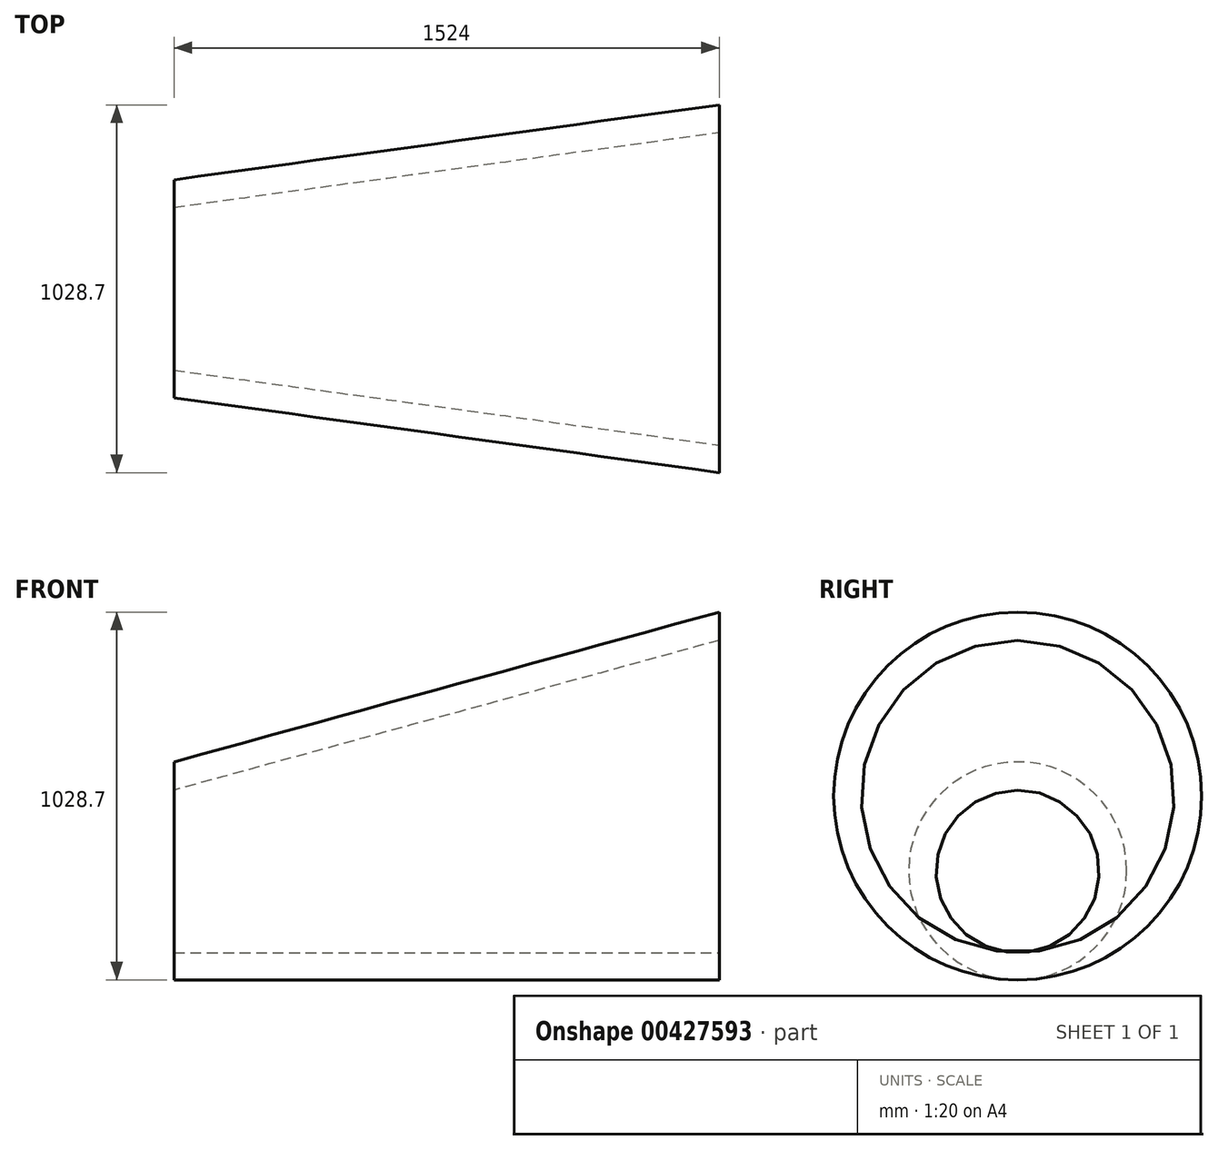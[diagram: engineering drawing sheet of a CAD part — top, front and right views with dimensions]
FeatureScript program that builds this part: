
annotation { "Feature Type Name" : "Feature", "Feature Type Description" : "" }
export const myFeature = defineFeature(function(context is Context, id is Id, definition is map)
    precondition{}
    {
        {
            var Q0;
            Q0=qCreatedBy(makeId("Right.planeOp"),FACE);
            var sketch = newSketch(context, id + "F0", { "sketchPlane" : qUnion([Q0])});
            skCircle(sketch, "E0", {"center": v(0, 0) * mm, "radius": 304.8 * mm});
            skPoint(sketch, "E1", {"position": v(0, -304.8) * mm});
            skLineSegment(sketch, "E2", {"start": v(0, 0) * mm, "end": v(0, -304.8) * mm, "construction": true});
            skSolve(sketch);
        }
        {
            var Q0;
            Q0=makeQuery(id+"F0.imprint","IMPRINT",FACE,{"disambiguationData":[TD([[makeQuery(id+"F0.imprint","IMPRINT",EDGE,{"derivedFrom":sQuery(id+"F0.wireOp",EDGE,"E0")}),1.0]])]});
            cPlane(context, id + "F1", {"entities" : qUnion([Q0]), "cplaneType" : CPlaneType.OFFSET, "offset" : 1524 * mm, "width" : 152.4 * mm, "height" : 152.4 * mm});
        }
        {
            var Q0;
            Q0=qCreatedBy(id+"F1.planeOp",FACE);
            var sketch = newSketch(context, id + "F2", { "sketchPlane" : qUnion([Q0])});
            skCircle(sketch, "E3", {"center": v(0, 209.55) * mm, "radius": 514.35 * mm});
            skLineSegment(sketch, "E4", {"start": v(0, -304.8) * mm, "end": v(0, 209.55) * mm, "construction": true});
            skSolve(sketch);
        }
        {
            var Q0;
            Q0=makeQuery(id+"F2.imprint","IMPRINT",FACE,{"disambiguationData":[TD([[makeQuery(id+"F2.imprint","IMPRINT",EDGE,{"derivedFrom":sQuery(id+"F2.wireOp",EDGE,"E3")}),1.0]])]});
            var Q1;
            Q1=makeQuery(id+"F0.imprint","IMPRINT",FACE,{"disambiguationData":[TD([[makeQuery(id+"F0.imprint","IMPRINT",EDGE,{"derivedFrom":sQuery(id+"F0.wireOp",EDGE,"E0")}),1.0]])]});
            loft(context, id + "F3", {"sheetProfilesArray" : [{ "sheetProfileEntities" : qUnion([Q0]) }, { "sheetProfileEntities" : qUnion([Q1]) }]});
        }
        {
            var Q0;
            Q0=makeQuery(id+"F3.opLoft","CAP_FACE",FACE,{"disambiguationData":[OSD([makeQuery(id+"F2.imprint","IMPRINT",FACE,{"disambiguationData":[TD([[makeQuery(id+"F2.imprint","IMPRINT",EDGE,{"derivedFrom":sQuery(id+"F2.wireOp",EDGE,"E3")}),1.0]])]})])],"isStart":true});
            var Q1;
            Q1=makeQuery(id+"F3.opLoft","CAP_FACE",FACE,{"disambiguationData":[OSD([makeQuery(id+"F0.imprint","IMPRINT",FACE,{"disambiguationData":[TD([[makeQuery(id+"F0.imprint","IMPRINT",EDGE,{"derivedFrom":sQuery(id+"F0.wireOp",EDGE,"E0")}),1.0]])]})])],"isStart":true});
            shell(context, id + "F4", {"entities" : qUnion([Q0, Q1]), "thickness" : 76.2 * mm});
        }
    });
